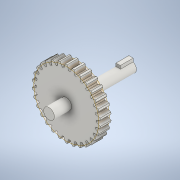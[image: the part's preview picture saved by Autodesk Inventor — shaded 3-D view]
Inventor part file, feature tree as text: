
AUTODESK INVENTOR PART (.ipt)
format: ipt  version: 2021 (Build 250183000, 183)  size: 552,960 bytes
history: native  units: mm (DEFAULTED — no unit token found)
features: sketch x6, extrude x4, plane x3, other x3, emboss x1
ambient origin geometry x8: Origin, YZ Plane, XZ Plane, XY Plane, X Axis, Y Axis, Z Axis, Center Point
bodies: Solid1 (feature_tree)
feature tree (17):
  extrude  "Extrusion1"  Depth=5.0mm TaperAngle=0.0deg
  plane  "Work Plane2"
  plane  "Work Plane8"
  plane  "Work Plane9"
  other  "Spur Gear"
  extrude  "Extrusion4"  Depth=10.0mm TaperAngle=0.0deg
  extrude  "Extrusion5"  Depth=1.047198mm TaperAngle=0.0deg
  extrude  "Extrusion6"  TaperAngle=0.0deg  [1 undecoded]
  emboss  "Emboss1"
  sketch  "Sketch1"  dims[d0=31.6mm d1=5.0mm d2=0.0mm]
  sketch  "Sketch2"  dims[d3=30.0mm d4=10.0mm d5=0.0mm]
  other  "Srf1"
  sketch  "Sketch6"  dims[d16=22.5mm d17=0.0mm d34=1.047198mm]
  sketch  "Sketch7"  dims[d39=0.0mm d41=0.0mm]
  sketch  "Sketch8"  dims[d43=22.5mm]
  sketch  "Sketch9"  dims[d46=22.5mm d47=0.0mm d48=0.0mm d68=5.0mm d73=25.0mm d74=0.0mm d75=2.0mm d76=1.5mm d77=6.0mm d78=0.0mm d79=5.0mm d80=8.0mm d81=0.0mm d82=1.0mm d83=0.0mm d59=0.5mm d60=0.872665mm d61=0.5mm d62=0.872665mm]
  other  "Pitch Diameter"
note: 1 required parameter value undecoded (feature->parameter linkage not recoverable at this tier; creation-order binding heuristic only, values carry confidence <= 0.55)
